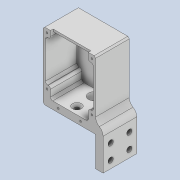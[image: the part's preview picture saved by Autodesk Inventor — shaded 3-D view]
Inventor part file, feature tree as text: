
AUTODESK INVENTOR PART (.ipt)
format: ipt  version: 2020 (Build 240168000, 168)  size: 227,328 bytes
history: native  units: mm
features: sketch x8, extrude x6, hole x2, fillet x2, chamfer x1
ambient origin geometry x8: Origin, YZ Plane, XZ Plane, XY Plane, X Axis, Y Axis, Z Axis, Center Point
bodies: Solid1 (feature_tree)
feature tree (19):
  extrude  "Extrusion1"  Depth=90.0mm
  extrude  "Extrusion2"  Depth=9.7mm
  extrude  "Extrusion3"  Depth=10.0mm
  hole  "Hole2"  [1 undecoded]
  hole  "Hole3"  [1 undecoded]
  extrude  "Extrusion4"  Depth=10.0mm
  fillet  "Fillet1"  Radius=10.0mm
  chamfer  "Chamfer2"  Distance=40.0mm
  extrude  "Extrusion5"  Depth=7.0mm
  extrude  "Extrusion6"  Depth=7.0mm
  fillet  "Fillet2"  Radius=10.0mm
  sketch  "Sketch1"  dims[d0=70.0mm d1=90.0mm]
  sketch  "Sketch2"  dims[d2=45.0mm d3=0.0mm d4=9.7mm]
  sketch  "Sketch3"  dims[d5=9.7mm d6=10.0mm]
  sketch  "Sketch5"  dims[d7=3.0mm d8=42.0mm d9=0.0mm]
  sketch  "Sketch6"  dims[d10=3.5mm d11=38.0mm d12=0.0mm]
  sketch  "Sketch8"  dims[d23=2.459mm d24=6.0mm d25=7.0mm d26=2.0mm d27=90.0deg d28=30.0mm d29=20.594885mm d30=10.0mm d31=10.0mm]
  sketch  "Sketch9"  dims[d33=6.0mm d34=6.0mm d35=12.0mm d36=2.0mm d37=90.0deg d38=30.0mm d39=20.594885mm]
  sketch  "Sketch10"  dims[d42=10.0mm d43=40.0mm d44=7.0mm d45=7.0mm d46=10.0mm d47=10.0mm d48=10.0mm d49=10.0mm d50=0.0mm d51=10.0mm d52=2.0mm d53=2.0mm d54=45.0deg d55=15.0mm d56=9.0mm d57=80.0mm d58=0.0mm d59=10.0mm d60=3.0mm d61=5.0mm d62=5.0mm d63=10.0mm d64=0.0mm d65=3.0mm]
note: 2 required parameter values undecoded (feature->parameter linkage not recoverable at this tier; creation-order binding heuristic only, values carry confidence <= 0.55)
